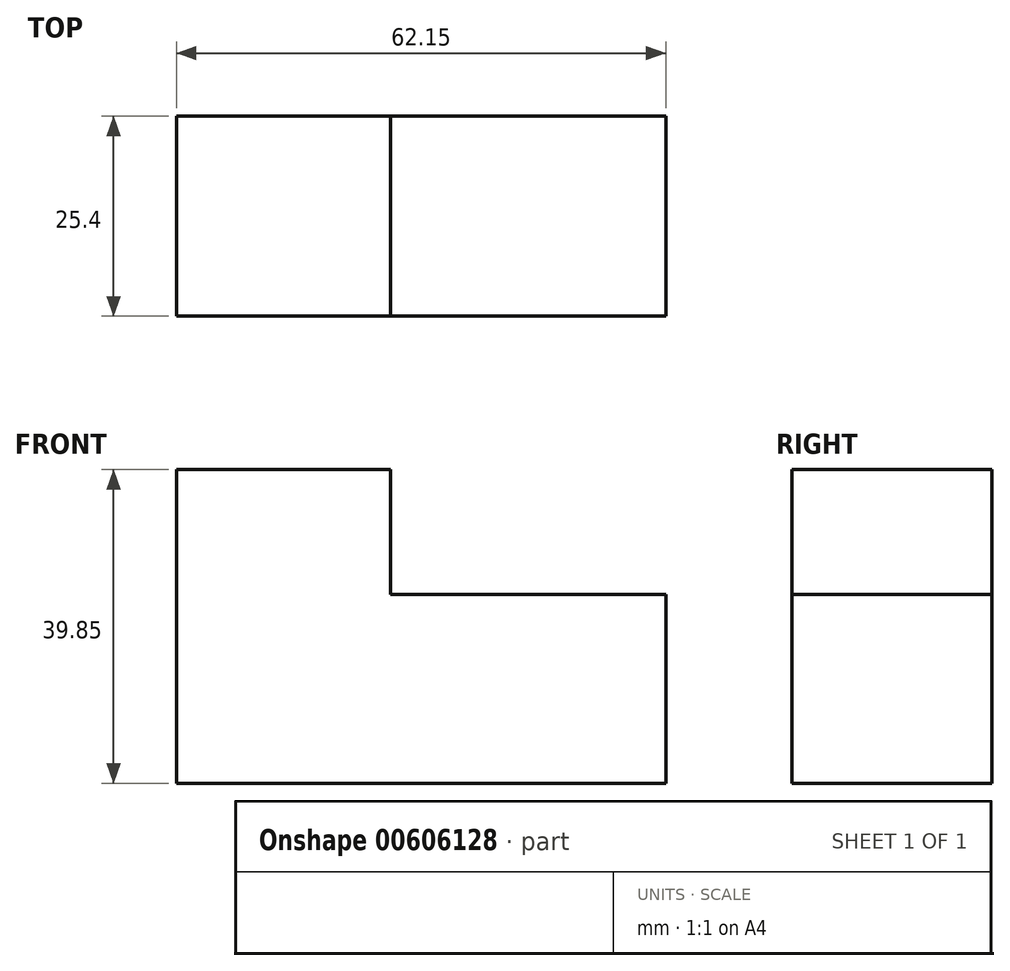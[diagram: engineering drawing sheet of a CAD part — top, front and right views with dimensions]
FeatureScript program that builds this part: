
annotation { "Feature Type Name" : "Feature", "Feature Type Description" : "" }
export const myFeature = defineFeature(function(context is Context, id is Id, definition is map)
    precondition{}
    {
        {
            var Q0;
            Q0=qCreatedBy(makeId("Front.planeOp"),FACE);
            var sketch = newSketch(context, id + "F0", { "sketchPlane" : qUnion([Q0])});
            skLineSegment(sketch, "E0", {"start": v(-62.15, 39.85) * mm, "end": v(-62.15, 0) * mm});
            skLineSegment(sketch, "E1", {"start": v(-62.15, 39.85) * mm, "end": v(-34.97, 39.85) * mm});
            skLineSegment(sketch, "E2", {"start": v(-34.97, 39.85) * mm, "end": v(-34.97, 23.97) * mm});
            skLineSegment(sketch, "E3", {"start": v(-34.97, 23.97) * mm, "end": v(0, 23.97) * mm});
            skLineSegment(sketch, "E4", {"start": v(-62.15, 0) * mm, "end": v(0, 0) * mm});
            skLineSegment(sketch, "E5", {"start": v(0, 23.97) * mm, "end": v(0, 0) * mm});
            skSolve(sketch);
        }
        {
            var Q0;
            Q0=makeQuery(id+"F0.imprint","IMPRINT",FACE,{"disambiguationData":[TD([[makeQuery(id+"F0.imprint","IMPRINT",EDGE,{"derivedFrom":sQuery(id+"F0.wireOp",EDGE,"E0")}),1.0]])]});
            extrude(context, id + "F1", {"entities" : qUnion([Q0]), "depth" : 25.4 * mm, "offsetDistance" : 25.4 * mm});
        }
    });
